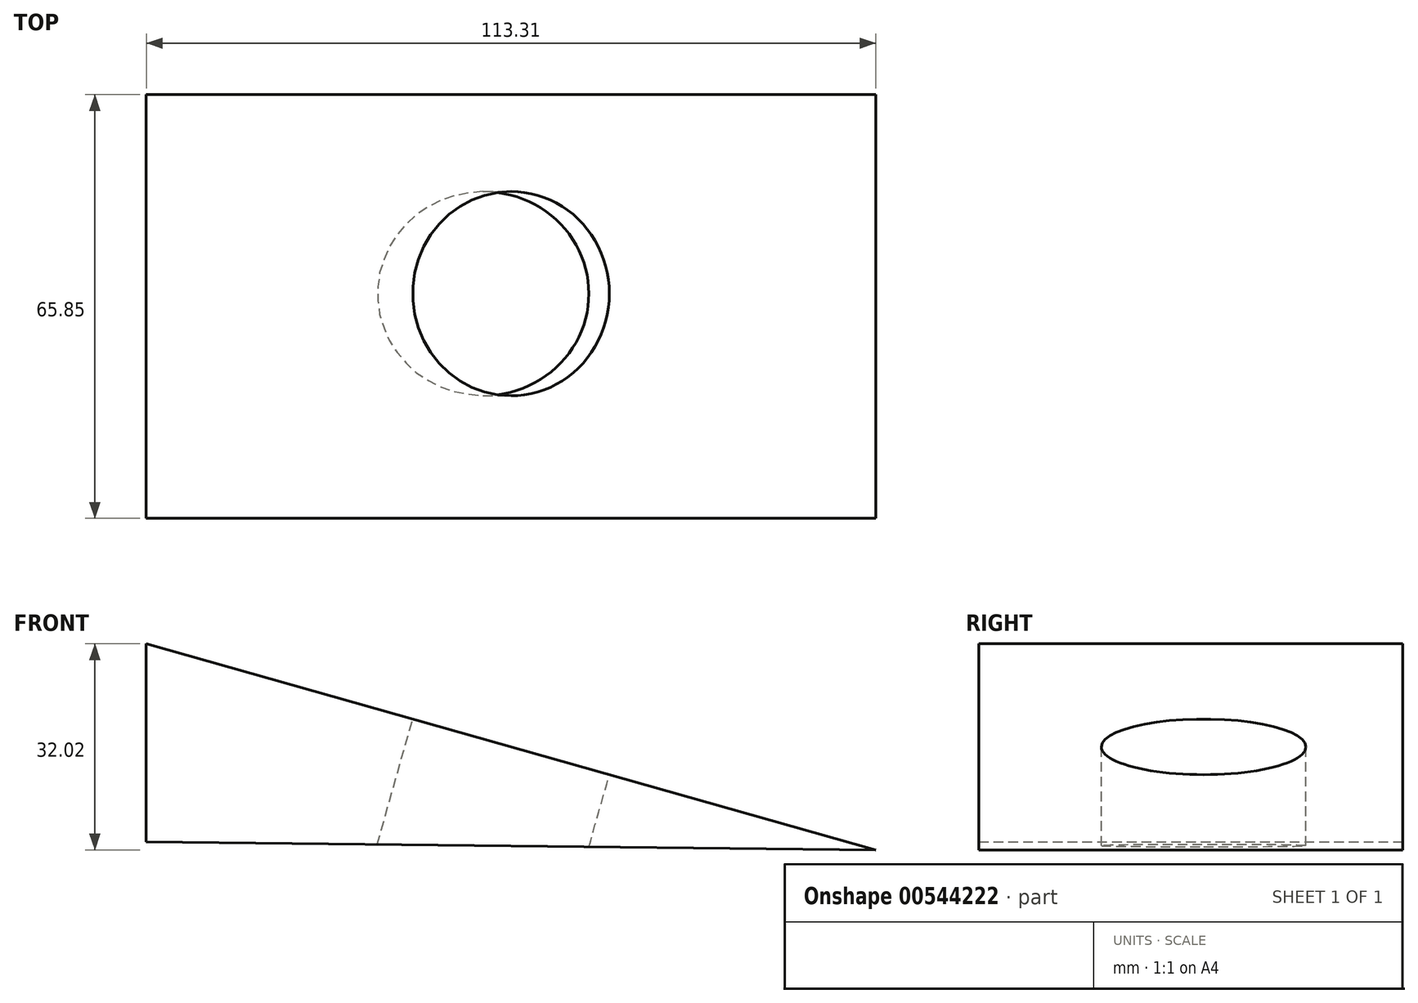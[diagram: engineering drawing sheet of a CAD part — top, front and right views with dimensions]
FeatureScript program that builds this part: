
annotation { "Feature Type Name" : "Feature", "Feature Type Description" : "" }
export const myFeature = defineFeature(function(context is Context, id is Id, definition is map)
    precondition{}
    {
        {
            var Q0;
            Q0=qCreatedBy(makeId("Front.planeOp"),FACE);
            var sketch = newSketch(context, id + "F0", { "sketchPlane" : qUnion([Q0])});
            skLineSegment(sketch, "E0", {"start": v(-56.01, 79.35) * mm, "end": v(-56.01, 48.55) * mm});
            skLineSegment(sketch, "E1", {"start": v(-56.01, 48.55) * mm, "end": v(57.3, 47.33) * mm});
            skLineSegment(sketch, "E2", {"start": v(57.3, 47.33) * mm, "end": v(-56.01, 79.35) * mm});
            skSolve(sketch);
        }
        {
            var Q0;
            Q0=makeQuery(id+"F0.imprint","IMPRINT",FACE,{"disambiguationData":[TD([[makeQuery(id+"F0.imprint","IMPRINT",EDGE,{"derivedFrom":sQuery(id+"F0.wireOp",EDGE,"E0")}),1.0]])]});
            extrude(context, id + "F1", {"entities" : qUnion([Q0]), "depth" : 65.85 * mm, "offsetDistance" : 25.4 * mm});
        }
        {
            var Q0;
            Q0=makeQuery(id+"F1.opExtrude","SWEPT_FACE",FACE,{"disambiguationData":[OSD([sQuery(id+"F0.wireOp",EDGE,"E2")])]});
            var sketch = newSketch(context, id + "F2", { "sketchPlane" : qUnion([Q0])});
            skCircle(sketch, "E3", {"center": v(-16.61, -30.93) * mm, "radius": 15.88 * mm});
            skPoint(sketch, "E3.centerSnap0", {"position": v(-16.61, 0) * mm});
            skSolve(sketch);
        }
        {
            var Q0;
            Q0=makeQuery(id+"F2.imprint","IMPRINT",FACE,{"disambiguationData":[TD([[makeQuery(id+"F2.imprint","IMPRINT",EDGE,{"derivedFrom":sQuery(id+"F2.wireOp",EDGE,"E3")}),1.0]])]});
            extrude(context, id + "F3", {"entities" : qUnion([Q0]), "operationType" : NewBodyOperationType.REMOVE, "oppositeDirection" : true, "depth" : 49.7 * mm, "offsetDistance" : 25.4 * mm});
        }
    });
